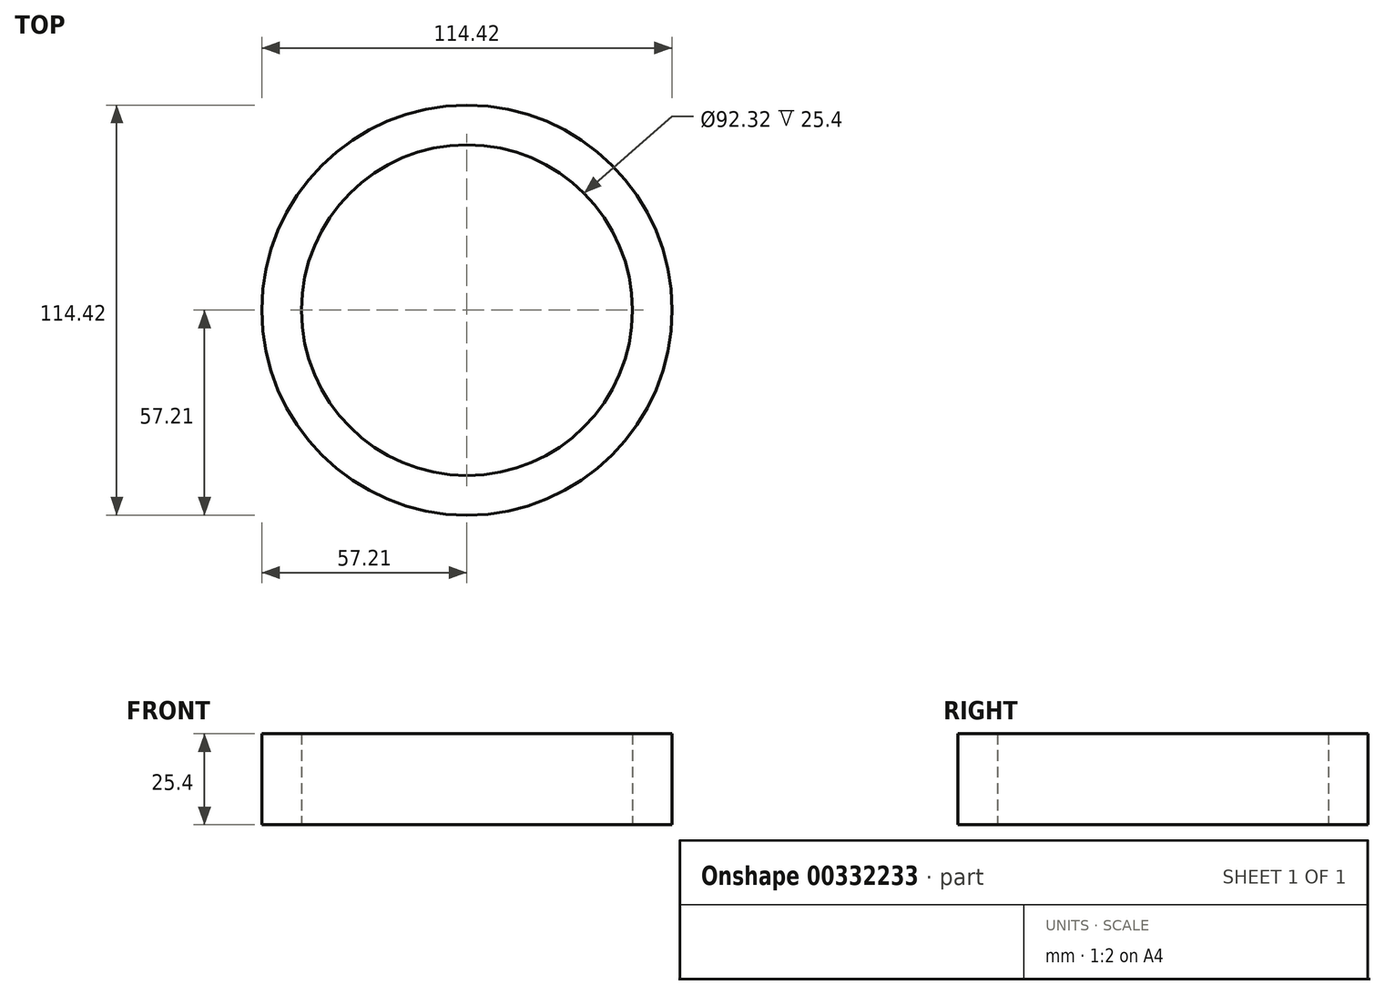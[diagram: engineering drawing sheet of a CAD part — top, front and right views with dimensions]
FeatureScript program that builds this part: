
annotation { "Feature Type Name" : "Feature", "Feature Type Description" : "" }
export const myFeature = defineFeature(function(context is Context, id is Id, definition is map)
    precondition{}
    {
        {
            var Q0;
            Q0=qCreatedBy(makeId("Top.planeOp"),FACE);
            var sketch = newSketch(context, id + "F0", { "sketchPlane" : qUnion([Q0])});
            skCircle(sketch, "E0", {"center": v(0, 0) * mm, "radius": 57.21 * mm});
            skSolve(sketch);
        }
        {
            var Q0;
            Q0 = qSketchRegion(id + "F0", true);
            extrude(context, id + "F1", {"entities" : qUnion([Q0]), "depth" : 25.4 * mm});
        }
        {
            var Q0;
            Q0=qCreatedBy(makeId("Top.planeOp"),FACE);
            var sketch = newSketch(context, id + "F2", { "sketchPlane" : qUnion([Q0])});
            skCircle(sketch, "E1", {"center": v(0, 0) * mm, "radius": 46.16 * mm});
            skSolve(sketch);
        }
        {
            var Q0;
            Q0 = qSketchRegion(id + "F2", true);
            extrude(context, id + "F3", {"entities" : qUnion([Q0]), "operationType" : NewBodyOperationType.REMOVE, "depth" : 25.4 * mm});
        }
        {
            var Q0;
            Q0=qCreatedBy(makeId("Top.planeOp"),FACE);
            var sketch = newSketch(context, id + "F4", { "sketchPlane" : qUnion([Q0])});
            skLineSegment(sketch, "E2.bottom", {"start": v(6.54, 171.55) * mm, "end": v(-6.54, 171.55) * mm});
            skLineSegment(sketch, "E2.top", {"start": v(6.54, 194.42) * mm, "end": v(-6.54, 194.42) * mm});
            skLineSegment(sketch, "E2.left", {"start": v(6.54, 171.55) * mm, "end": v(6.54, 194.42) * mm});
            skLineSegment(sketch, "E2.right", {"start": v(-6.54, 171.55) * mm, "end": v(-6.54, 194.42) * mm});
            skPoint(sketch, "E2.middle", {"position": v(0, 182.99) * mm});
            skSolve(sketch);
        }
        {
            var Q0;
            Q0 = qSketchRegion(id + "F4", true);
            extrude(context, id + "F5", {"entities" : qUnion([Q0]), "operationType" : NewBodyOperationType.REMOVE, "depth" : 25.4 * mm});
        }
    });
